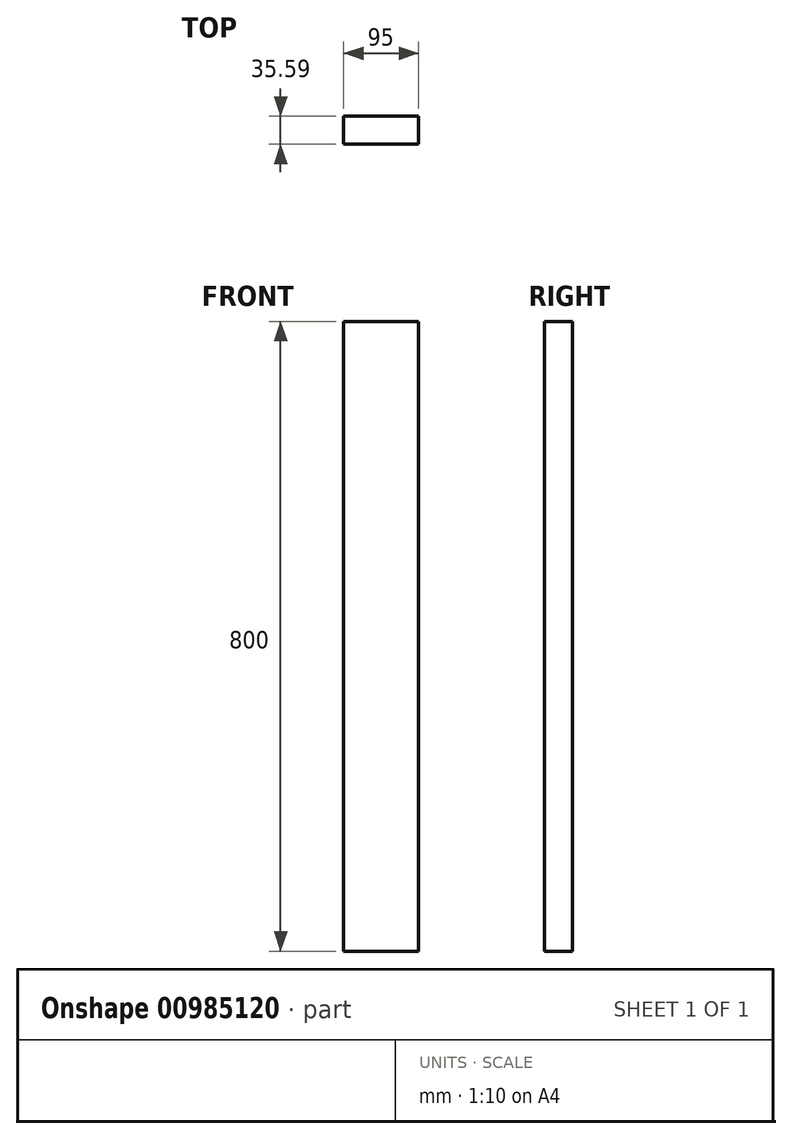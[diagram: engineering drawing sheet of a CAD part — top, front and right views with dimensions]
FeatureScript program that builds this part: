
annotation { "Feature Type Name" : "Feature", "Feature Type Description" : "" }
export const myFeature = defineFeature(function(context is Context, id is Id, definition is map)
    precondition{}
    {
        {
            var Q0;
            Q0=qCreatedBy(makeId("Top.planeOp"),FACE);
            var sketch = newSketch(context, id + "F0", { "sketchPlane" : qUnion([Q0])});
            skLineSegment(sketch, "E0.bottom", {"start": v(-97.33, 0) * mm, "end": v(-2.33, 0) * mm});
            skLineSegment(sketch, "E0.top", {"start": v(-97.33, -35.6) * mm, "end": v(-2.33, -35.6) * mm});
            skLineSegment(sketch, "E0.left", {"start": v(-97.33, 0) * mm, "end": v(-97.33, -35.6) * mm});
            skLineSegment(sketch, "E0.right", {"start": v(-2.33, 0) * mm, "end": v(-2.33, -35.6) * mm});
            skSolve(sketch);
        }
        {
            var Q0;
            Q0 = qSketchRegion(id + "F0", true);
            extrude(context, id + "F1", {"entities" : qUnion([Q0]), "depth" : 800 * mm, "offsetDistance" : 25 * mm});
        }
    });
